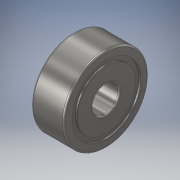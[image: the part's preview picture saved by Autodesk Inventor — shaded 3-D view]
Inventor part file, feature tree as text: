
AUTODESK INVENTOR PART (.ipt)
format: ipt  version: 2018 (Build 220112000, 112)  size: 160,768 bytes
history: native  units: in
note: dims shown in document units (in); Inventor stores cm internally (conversion verified against a paired STEP export)
features: extrude x2, fillet x2, sketch x2, mirror x1
ambient origin geometry x8: Origin, YZ Plane, XZ Plane, XY Plane, X Axis, Y Axis, Z Axis, Center Point
bodies: Solid1 (feature_tree)
feature tree (7):
  extrude  "Extrusion1"  Depth=0.0098in
  fillet  "Fillet1"  Radius=0.1969in
  fillet  "Fillet2"  Radius=0.0098in
  extrude  "Extrusion2"  Depth=0.0098in
  mirror  "Mirror1"
  sketch  "Sketch1"  dims[d0=0.5118in d1=0.1575in d2=0.1969in d3=0.0in d4=0.0098in]
  sketch  "Sketch2"  dims[d5=0.0098in d6=0.4134in d7=0.3543in d8=0.0098in d9=0.0in]
